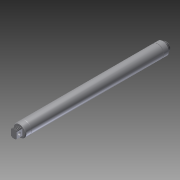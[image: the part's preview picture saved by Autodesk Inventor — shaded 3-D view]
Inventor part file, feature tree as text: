
AUTODESK INVENTOR PART (.ipt)
format: ipt  version: 2012 (Build 160160000, 160)  size: 152,064 bytes
history: native  units: in
note: dims shown in document units (in); Inventor stores cm internally (conversion verified against a paired STEP export)
features: extrude x7, sketch x3, thread x3, fillet x2, chamfer x2
ambient origin geometry x8: Origin, YZ Plane, XZ Plane, XY Plane, X Axis, Y Axis, Z Axis, Center Point
bodies: Solid1 (feature_tree)
feature tree (17):
  sketch  "Sketch1"  dims[d2=1.0in d3=1.125in d4=0.5in]
  extrude  "Extrusion1"  Depth=1.125in
  fillet  "Fillet1"  Radius=0.5in
  extrude  "Extrusion2"  Depth=0.559in
  extrude  "Extrusion3"  Depth=0.375in
  chamfer  "Chamfer1"  Distance=12.0in
  thread  "Thread1"  [1 undecoded]
  thread  "Thread2"  [1 undecoded]
  sketch  "Sketch2"  dims[d5=0.25in d6=0.559in]
  extrude  "Extrusion4"  Depth=1.0in TaperAngle=0.0deg
  extrude  "Extrusion5"  Depth=0.0625in TaperAngle=45.0deg
  fillet  "Fillet2"  Radius=1.0in
  extrude  "Extrusion6"  Depth=1.0in TaperAngle=0.0deg
  chamfer  "Chamfer2"  Distance=0.75in
  thread  "Thread3"  [1 undecoded]
  extrude  "Extrusion7"  Depth=0.25in
  sketch  "Sketch3"  dims[d7=0.2795in d8=0.375in d10=12.0in d11=0.0in d12=0.0312in d13=0.5in d14=0.0in d15=1.0in d16=0.0in d17=0.0625in d18=0.125in d19=45.0deg d20=1.0in d21=0.0in d22=1.0in d23=0.0in d24=0.75in d25=0.3125in d26=0.25in d27=0.5in d28=0.0in d29=0.75in d30=0.0in d31=0.0075in d32=0.75in d33=0.0in d34=0.0625in d35=0.125in d36=45.0deg d37=1.0in d38=0.0in d39=0.25in d40=0.2795in d41=0.559in d42=0.25in d43=1.0in d44=0.0in]
note: 3 required parameter values undecoded (feature->parameter linkage not recoverable at this tier; creation-order binding heuristic only, values carry confidence <= 0.55)
